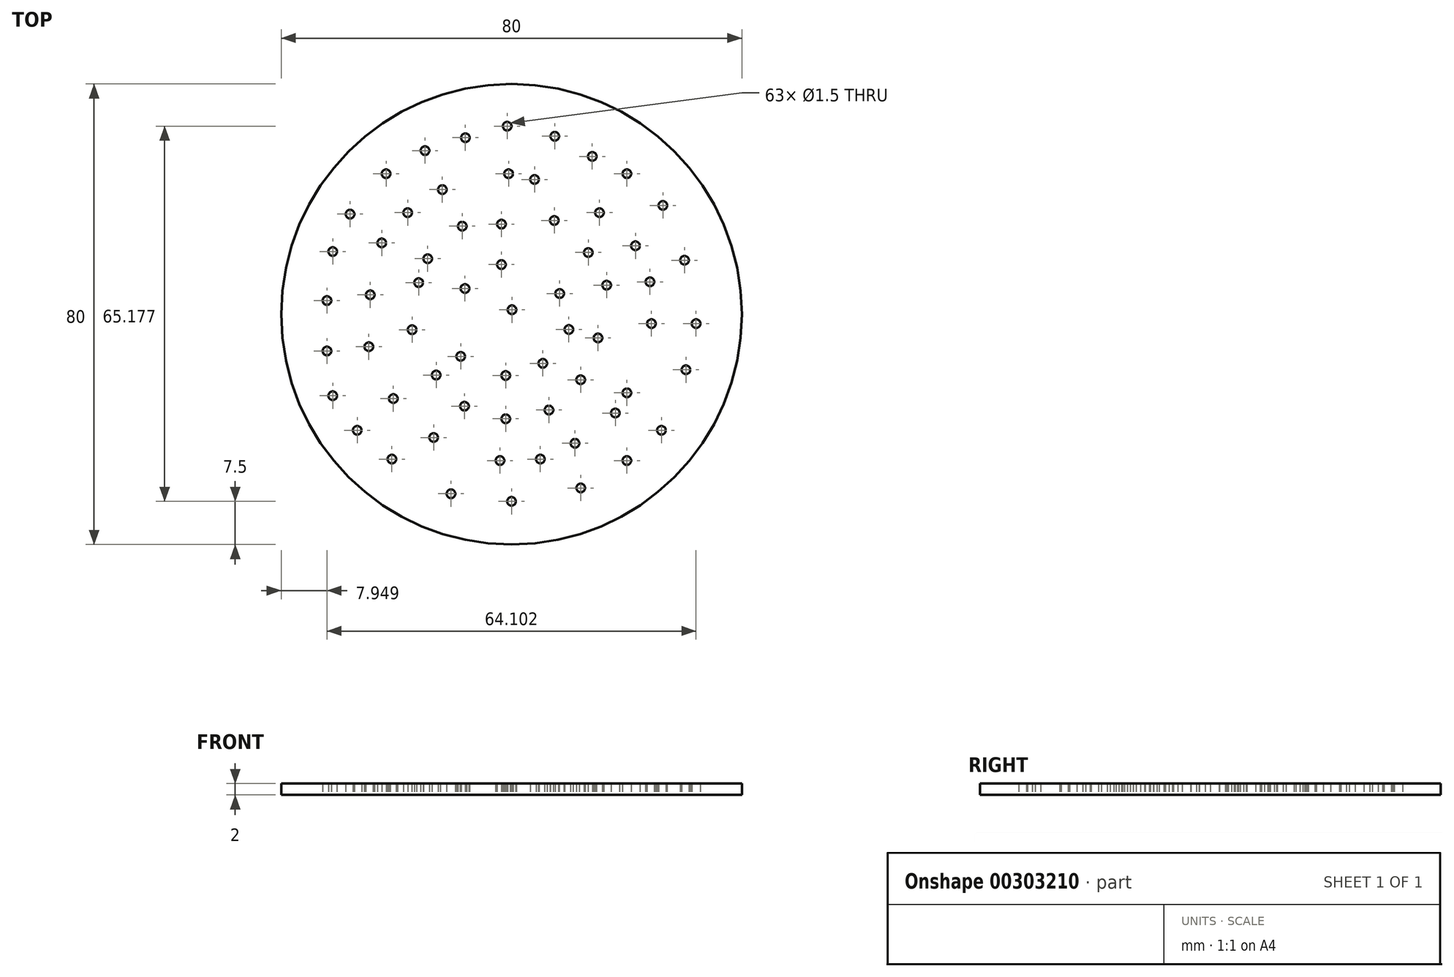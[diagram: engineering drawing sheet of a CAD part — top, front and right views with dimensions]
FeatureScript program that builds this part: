
annotation { "Feature Type Name" : "Feature", "Feature Type Description" : "" }
export const myFeature = defineFeature(function(context is Context, id is Id, definition is map)
    precondition{}
    {
        {
            var Q0;
            Q0=qCreatedBy(makeId("Top.planeOp"),FACE);
            var sketch = newSketch(context, id + "F0", { "sketchPlane" : qUnion([Q0])});
            skCircle(sketch, "E0", {"center": v(0, 0) * mm, "radius": 40 * mm});
            skCircle(sketch, "E1", {"center": v(0, 0) * mm, "radius": 32.5 * mm, "construction": true});
            skCircle(sketch, "E2", {"center": v(0, 0) * mm, "radius": 25 * mm, "construction": true});
            skCircle(sketch, "E3", {"center": v(0, 0) * mm, "radius": 17.5 * mm, "construction": true});
            skCircle(sketch, "E4", {"center": v(0, 0) * mm, "radius": 10 * mm, "construction": true});
            skCircle(sketch, "E5", {"center": v(0, 0) * mm, "radius": 2.5 * mm, "construction": true});
            skCircle(sketch, "E6", {"center": v(0, -32.5) * mm, "radius": 0.75 * mm});
            skCircle(sketch, "E7", {"center": v(-0.75, 32.68) * mm, "radius": 0.75 * mm});
            skCircle(sketch, "E8", {"center": v(-0.5, 24.41) * mm, "radius": 0.75 * mm});
            skCircle(sketch, "E9", {"center": v(-1.75, 15.65) * mm, "radius": 0.75 * mm});
            skCircle(sketch, "E10", {"center": v(-1.75, 8.64) * mm, "radius": 0.75 * mm});
            skCircle(sketch, "E11", {"center": v(-1, -10.64) * mm, "radius": 0.75 * mm});
            skCircle(sketch, "E12", {"center": v(-1, -18.15) * mm, "radius": 0.75 * mm});
            skCircle(sketch, "E13", {"center": v(-2, -25.42) * mm, "radius": 0.75 * mm});
            skCircle(sketch, "E14", {"center": v(-20.78, -25.16) * mm, "radius": 0.75 * mm});
            skCircle(sketch, "E15", {"center": v(-10.52, -31.17) * mm, "radius": 0.75 * mm});
            skCircle(sketch, "E16", {"center": v(-26.8, -20.16) * mm, "radius": 0.75 * mm});
            skCircle(sketch, "E17", {"center": v(-31.05, -14.15) * mm, "radius": 0.75 * mm});
            skCircle(sketch, "E18", {"center": v(-32.05, -6.39) * mm, "radius": 0.75 * mm});
            skCircle(sketch, "E19", {"center": v(-32.05, 2.38) * mm, "radius": 0.75 * mm});
            skCircle(sketch, "E20", {"center": v(-31.05, 10.9) * mm, "radius": 0.75 * mm});
            skCircle(sketch, "E21", {"center": v(-28.04, 17.4) * mm, "radius": 0.75 * mm});
            skCircle(sketch, "E22", {"center": v(-21.78, 24.41) * mm, "radius": 0.75 * mm});
            skCircle(sketch, "E23", {"center": v(-15.02, 28.42) * mm, "radius": 0.75 * mm});
            skCircle(sketch, "E24", {"center": v(-8.01, 30.67) * mm, "radius": 0.75 * mm});
            skCircle(sketch, "E25", {"center": v(7.51, 30.92) * mm, "radius": 0.75 * mm});
            skCircle(sketch, "E26", {"center": v(14.02, 27.42) * mm, "radius": 0.75 * mm});
            skCircle(sketch, "E27", {"center": v(20.03, 24.41) * mm, "radius": 0.75 * mm});
            skCircle(sketch, "E28", {"center": v(26.3, 18.9) * mm, "radius": 0.75 * mm});
            skCircle(sketch, "E29", {"center": v(30.05, 9.39) * mm, "radius": 0.75 * mm});
            skCircle(sketch, "E30", {"center": v(32.05, -1.63) * mm, "radius": 0.75 * mm});
            skCircle(sketch, "E31", {"center": v(30.3, -9.64) * mm, "radius": 0.75 * mm});
            skCircle(sketch, "E32", {"center": v(26.04, -20.16) * mm, "radius": 0.75 * mm});
            skCircle(sketch, "E33", {"center": v(20.03, -25.42) * mm, "radius": 0.75 * mm});
            skCircle(sketch, "E34", {"center": v(12.02, -30.17) * mm, "radius": 0.75 * mm});
            skCircle(sketch, "E35", {"center": v(-13.52, -21.4) * mm, "radius": 0.75 * mm});
            skCircle(sketch, "E36", {"center": v(-20.53, -14.65) * mm, "radius": 0.75 * mm});
            skCircle(sketch, "E37", {"center": v(-24.79, -5.63) * mm, "radius": 0.75 * mm});
            skCircle(sketch, "E38", {"center": v(-24.54, 3.38) * mm, "radius": 0.75 * mm});
            skCircle(sketch, "E39", {"center": v(-22.54, 12.4) * mm, "radius": 0.75 * mm});
            skCircle(sketch, "E40", {"center": v(-18.03, 17.66) * mm, "radius": 0.75 * mm});
            skCircle(sketch, "E41", {"center": v(-12.02, 21.66) * mm, "radius": 0.75 * mm});
            skCircle(sketch, "E42", {"center": v(4, 23.41) * mm, "radius": 0.75 * mm});
            skCircle(sketch, "E43", {"center": v(15.27, 17.66) * mm, "radius": 0.75 * mm});
            skCircle(sketch, "E44", {"center": v(21.54, 11.9) * mm, "radius": 0.75 * mm});
            skCircle(sketch, "E45", {"center": v(24.04, 5.64) * mm, "radius": 0.75 * mm});
            skCircle(sketch, "E46", {"center": v(24.3, -1.63) * mm, "radius": 0.75 * mm});
            skCircle(sketch, "E47", {"center": v(20.04, -13.65) * mm, "radius": 0.75 * mm});
            skCircle(sketch, "E48", {"center": v(18.03, -17.15) * mm, "radius": 0.75 * mm});
            skCircle(sketch, "E49", {"center": v(11.02, -22.4) * mm, "radius": 0.75 * mm});
            skCircle(sketch, "E50", {"center": v(5, -25.15) * mm, "radius": 0.75 * mm});
            skCircle(sketch, "E51", {"center": v(6.5, -16.63) * mm, "radius": 0.75 * mm});
            skCircle(sketch, "E52", {"center": v(12.01, -11.37) * mm, "radius": 0.75 * mm});
            skCircle(sketch, "E53", {"center": v(15.01, -4.1) * mm, "radius": 0.75 * mm});
            skCircle(sketch, "E54", {"center": v(-16.12, 5.5) * mm, "radius": 0.75 * mm});
            skCircle(sketch, "E55", {"center": v(-13.09, -10.56) * mm, "radius": 0.75 * mm});
            skCircle(sketch, "E56", {"center": v(-8.82, -7.31) * mm, "radius": 0.75 * mm});
            skCircle(sketch, "E57", {"center": v(-8.09, 4.47) * mm, "radius": 0.75 * mm});
            skCircle(sketch, "E58", {"center": v(5.43, -8.52) * mm, "radius": 0.75 * mm});
            skCircle(sketch, "E59", {"center": v(9.96, -2.64) * mm, "radius": 0.75 * mm});
            skCircle(sketch, "E60", {"center": v(8.36, 3.6) * mm, "radius": 0.75 * mm});
            skCircle(sketch, "E61", {"center": v(7.43, 16.3) * mm, "radius": 0.75 * mm});
            skCircle(sketch, "E62", {"center": v(13.34, 10.73) * mm, "radius": 0.75 * mm});
            skCircle(sketch, "E63", {"center": v(16.52, 5.05) * mm, "radius": 0.75 * mm});
            skCircle(sketch, "E64", {"center": v(-8.56, 15.31) * mm, "radius": 0.75 * mm});
            skCircle(sketch, "E65", {"center": v(-14.56, 9.66) * mm, "radius": 0.75 * mm});
            skCircle(sketch, "E66", {"center": v(-17.27, -2.7) * mm, "radius": 0.75 * mm});
            skCircle(sketch, "E67", {"center": v(-8.17, -15.97) * mm, "radius": 0.75 * mm});
            skCircle(sketch, "E68", {"center": v(0.08, 0.78) * mm, "radius": 0.75 * mm});
            skSolve(sketch);
        }
        {
            var Q0;
            Q0=makeQuery(id+"F0.imprint","IMPRINT",FACE,{"disambiguationData":[TD([[makeQuery(id+"F0.imprint","IMPRINT",EDGE,{"derivedFrom":sQuery(id+"F0.wireOp",EDGE,"E0")}),1.0]])]});
            extrude(context, id + "F1", {"entities" : qUnion([Q0]), "depth" : 2 * mm});
        }
    });
